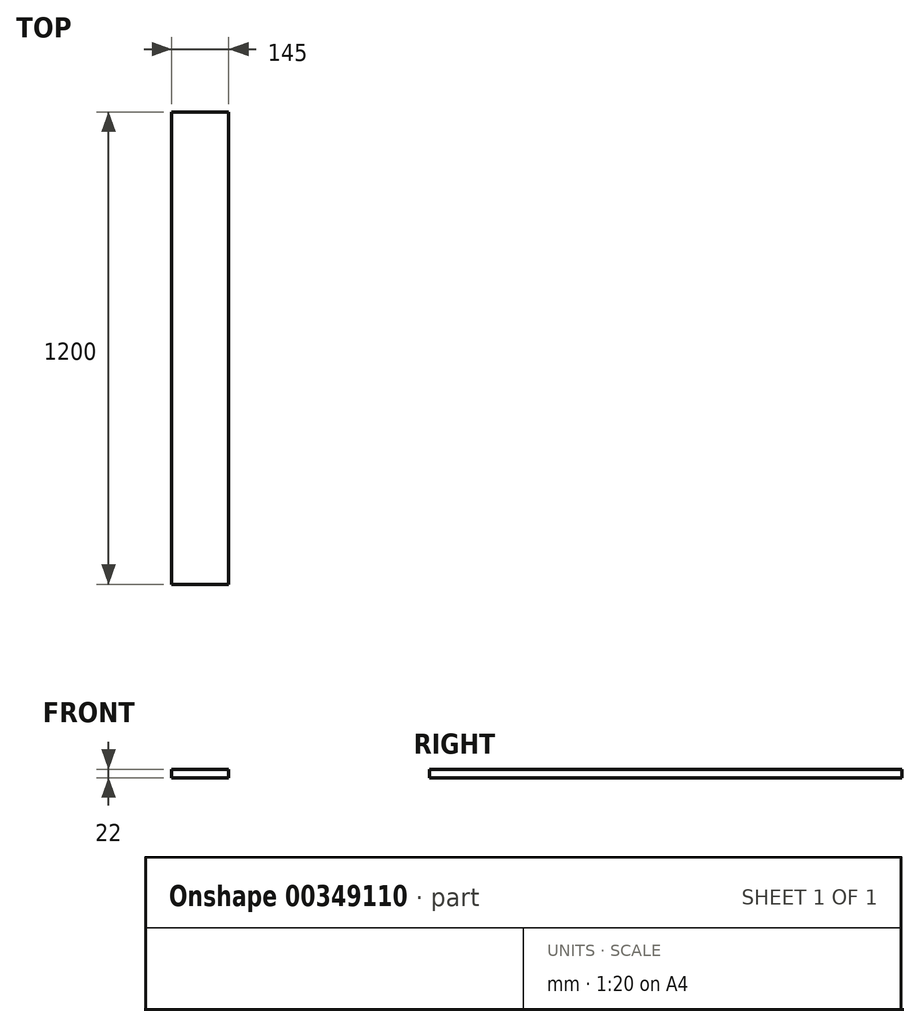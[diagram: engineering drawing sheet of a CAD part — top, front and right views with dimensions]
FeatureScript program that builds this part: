
annotation { "Feature Type Name" : "Feature", "Feature Type Description" : "" }
export const myFeature = defineFeature(function(context is Context, id is Id, definition is map)
    precondition{}
    {
        {
            var Q0;
            Q0=qCreatedBy(makeId("Top.planeOp"),FACE);
            var sketch = newSketch(context, id + "F0", { "sketchPlane" : qUnion([Q0])});
            skLineSegment(sketch, "E0.bottom", {"start": v(-72.5, 600) * mm, "end": v(72.5, 600) * mm});
            skLineSegment(sketch, "E0.top", {"start": v(-72.5, -600) * mm, "end": v(72.5, -600) * mm});
            skLineSegment(sketch, "E0.left", {"start": v(-72.5, 600) * mm, "end": v(-72.5, -600) * mm});
            skLineSegment(sketch, "E0.right", {"start": v(72.5, 600) * mm, "end": v(72.5, -600) * mm});
            skSolve(sketch);
        }
        {
            var Q0;
            Q0 = qSketchRegion(id + "F0", true);
            extrude(context, id + "F1", {"entities" : qUnion([Q0]), "endBound" : BoundingType.SYMMETRIC, "depth" : 22 * mm});
        }
    });
